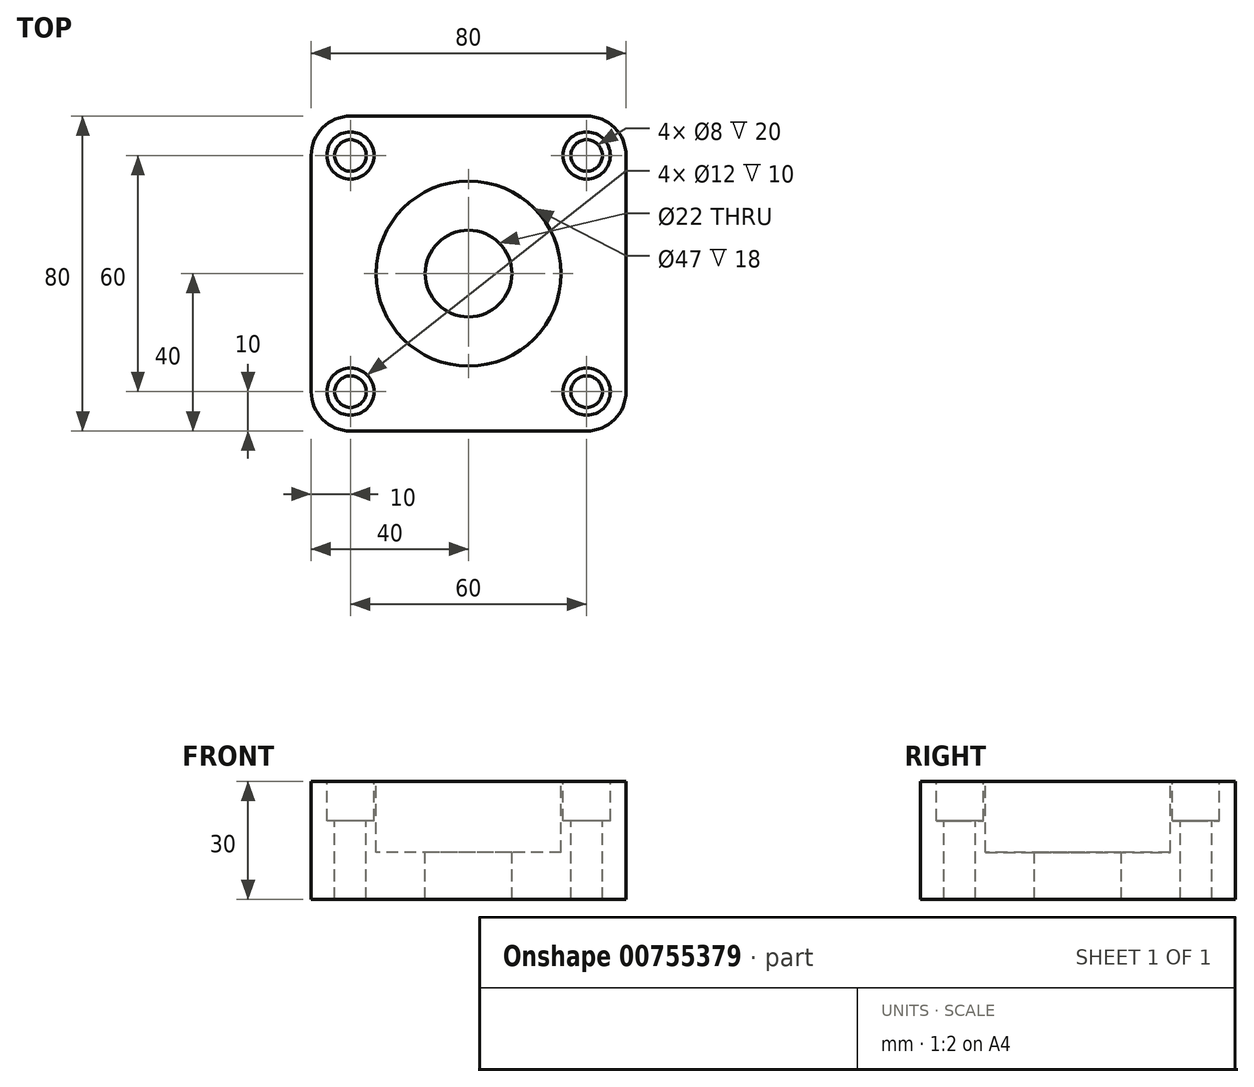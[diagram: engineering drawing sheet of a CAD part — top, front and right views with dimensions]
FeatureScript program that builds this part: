
annotation { "Feature Type Name" : "Feature", "Feature Type Description" : "" }
export const myFeature = defineFeature(function(context is Context, id is Id, definition is map)
    precondition{}
    {
        {
            var Q0;
            Q0=qCreatedBy(makeId("Top.planeOp"),FACE);
            var sketch = newSketch(context, id + "F0", { "sketchPlane" : qUnion([Q0])});
            skLineSegment(sketch, "E0.bottom", {"start": v(40, -40) * mm, "end": v(-40, -40) * mm});
            skLineSegment(sketch, "E0.top", {"start": v(40, 40) * mm, "end": v(-40, 40) * mm});
            skLineSegment(sketch, "E0.left", {"start": v(40, -40) * mm, "end": v(40, 40) * mm});
            skLineSegment(sketch, "E0.right", {"start": v(-40, -40) * mm, "end": v(-40, 40) * mm});
            skPoint(sketch, "E0.middle", {"position": v(0, 0) * mm});
            skSolve(sketch);
        }
        {
            var Q0;
            Q0=makeQuery(id+"F0.imprint","IMPRINT",FACE,{"disambiguationData":[TD([[makeQuery(id+"F0.imprint","IMPRINT",EDGE,{"derivedFrom":sQuery(id+"F0.wireOp",EDGE,"E0.bottom")}),-1.0]])]});
            extrude(context, id + "F1", {"entities" : qUnion([Q0]), "depth" : 30 * mm, "offsetDistance" : 25 * mm});
        }
        {
            var Q0;
            Q0=makeQuery(id+"F1.opExtrude","SWEPT_EDGE",EDGE,{"disambiguationData":[OSD([sQuery(id+"F0.wireOp",EDGE,"E0.top"),sQuery(id+"F0.wireOp",EDGE,"E0.right")])]});
            var Q1;
            Q1=makeQuery(id+"F1.opExtrude","SWEPT_EDGE",EDGE,{"disambiguationData":[OSD([sQuery(id+"F0.wireOp",EDGE,"E0.bottom"),sQuery(id+"F0.wireOp",EDGE,"E0.right")])]});
            var Q2;
            Q2=makeQuery(id+"F1.opExtrude","SWEPT_EDGE",EDGE,{"disambiguationData":[OSD([sQuery(id+"F0.wireOp",EDGE,"E0.bottom"),sQuery(id+"F0.wireOp",EDGE,"E0.left")])]});
            var Q3;
            Q3=makeQuery(id+"F1.opExtrude","SWEPT_EDGE",EDGE,{"disambiguationData":[OSD([sQuery(id+"F0.wireOp",EDGE,"E0.top"),sQuery(id+"F0.wireOp",EDGE,"E0.left")])]});
            fillet(context, id + "F2", {"entities" : qUnion([Q0, Q1, Q2, Q3]), "radius" : 10 * mm, "tangentPropagation" : true, "allowEdgeOverflow" : false});
        }
        {
            var Q0;
            Q0=makeQuery(id+"F1.opExtrude","CAP_FACE",FACE,{"disambiguationData":[OSD([sQuery(id+"F0.wireOp",EDGE,"E0.bottom"),sQuery(id+"F0.wireOp",EDGE,"E0.top"),sQuery(id+"F0.wireOp",EDGE,"E0.left"),sQuery(id+"F0.wireOp",EDGE,"E0.right")])],"isStart":false});
            var sketch = newSketch(context, id + "F3", { "sketchPlane" : qUnion([Q0])});
            skCircle(sketch, "E1", {"center": v(0, 0) * mm, "radius": 11 * mm});
            skSolve(sketch);
        }
        {
            var Q0;
            Q0=sQuery(id+"F3.wireOp",VERTEX,"E1.center");
            var Q1;
            Q1=makeQuery(id+"F1.opExtrude","SWEPT_BODY",BODY,{"disambiguationData":[OSD([sQuery(id+"F0.wireOp",EDGE,"E0.bottom"),sQuery(id+"F0.wireOp",EDGE,"E0.top"),sQuery(id+"F0.wireOp",EDGE,"E0.left"),sQuery(id+"F0.wireOp",EDGE,"E0.right")])]});
            hole(context, id + "F4", {"style" : HoleStyle.C_BORE, "endStyle" : HoleEndStyle.THROUGH, "holeDiameter" : 22 * mm, "cBoreDiameter" : 47 * mm, "cBoreDepth" : 18 * mm, "majorDiameter" : 5 * mm, "isTappedThrough" : true, "tappedDepth" : 12 * mm, "tapClearance" : 3, "locations" : qUnion([Q0]), "scope" : qUnion([Q1])});
        }
        {
            var Q0;
            Q0=makeQuery(id+"F1.opExtrude","CAP_FACE",FACE,{"disambiguationData":[OSD([sQuery(id+"F0.wireOp",EDGE,"E0.bottom"),sQuery(id+"F0.wireOp",EDGE,"E0.top"),sQuery(id+"F0.wireOp",EDGE,"E0.left"),sQuery(id+"F0.wireOp",EDGE,"E0.right")])],"isStart":false});
            var sketch = newSketch(context, id + "F5", { "sketchPlane" : qUnion([Q0])});
            skCircle(sketch, "E2", {"center": v(-30, 30) * mm, "radius": 5 * mm});
            skCircle(sketch, "E3", {"center": v(30, 30) * mm, "radius": 5 * mm});
            skCircle(sketch, "E4", {"center": v(-30, -30) * mm, "radius": 5 * mm});
            skCircle(sketch, "E5", {"center": v(30, -30) * mm, "radius": 5 * mm});
            skSolve(sketch);
        }
        {
            var Q0;
            Q0=sQuery(id+"F5.wireOp",VERTEX,"E2.center");
            var Q1;
            Q1=sQuery(id+"F5.wireOp",VERTEX,"E3.center");
            var Q2;
            Q2=sQuery(id+"F5.wireOp",VERTEX,"E5.center");
            var Q3;
            Q3=sQuery(id+"F5.wireOp",VERTEX,"E4.center");
            var Q4;
            Q4=makeQuery(id+"F1.opExtrude","SWEPT_BODY",BODY,{"disambiguationData":[OSD([sQuery(id+"F0.wireOp",EDGE,"E0.bottom"),sQuery(id+"F0.wireOp",EDGE,"E0.top"),sQuery(id+"F0.wireOp",EDGE,"E0.left"),sQuery(id+"F0.wireOp",EDGE,"E0.right")])]});
            hole(context, id + "F6", {"style" : HoleStyle.C_BORE, "endStyle" : HoleEndStyle.THROUGH, "holeDiameter" : 8 * mm, "cBoreDiameter" : 12 * mm, "cBoreDepth" : 10 * mm, "majorDiameter" : 5 * mm, "isTappedThrough" : true, "tappedDepth" : 12 * mm, "tapClearance" : 3, "locations" : qUnion([Q0, Q1, Q2, Q3]), "scope" : qUnion([Q4])});
        }
    });
